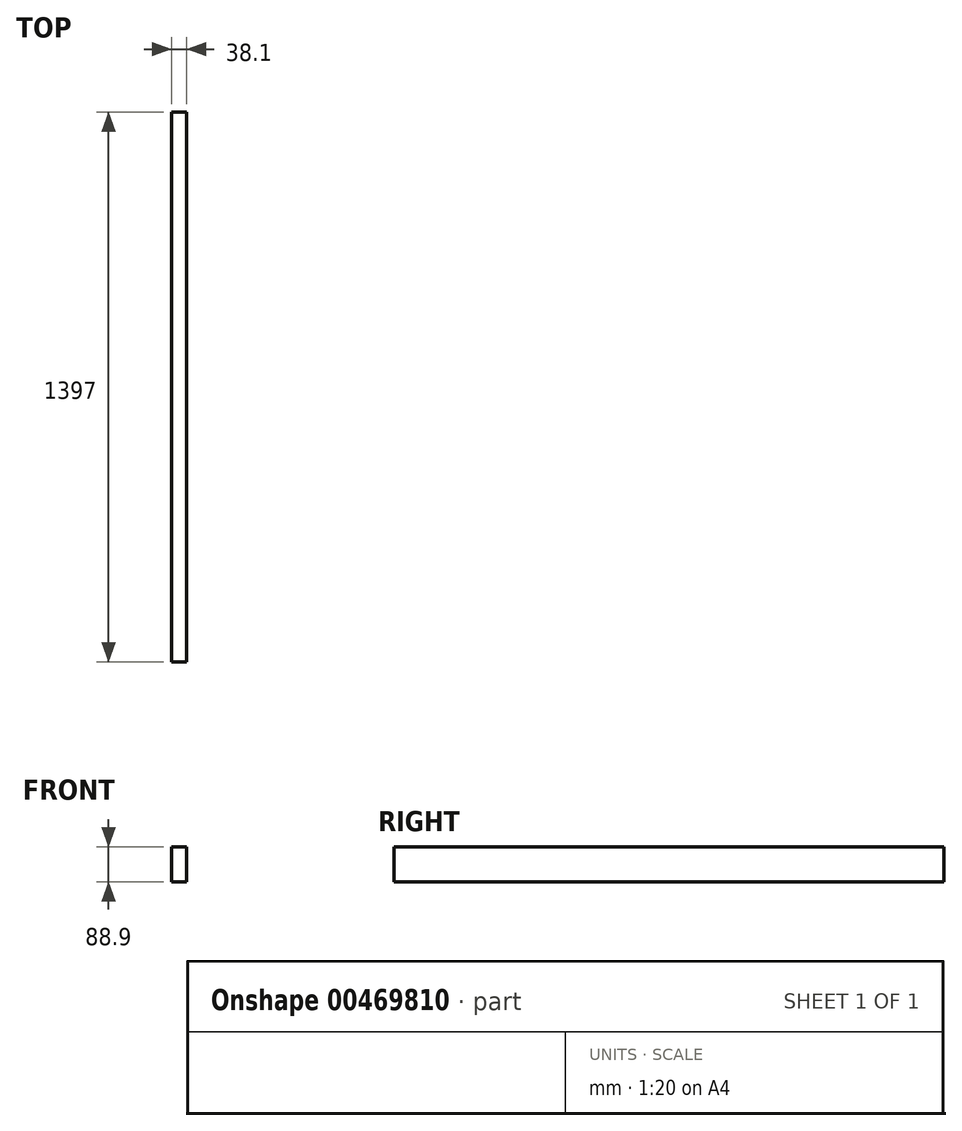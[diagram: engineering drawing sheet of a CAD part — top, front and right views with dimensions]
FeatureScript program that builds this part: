
annotation { "Feature Type Name" : "Feature", "Feature Type Description" : "" }
export const myFeature = defineFeature(function(context is Context, id is Id, definition is map)
    precondition{}
    {
        {
            var Q0;
            Q0=qCreatedBy(makeId("Front.planeOp"),FACE);
            var sketch = newSketch(context, id + "F0", { "sketchPlane" : qUnion([Q0])});
            skLineSegment(sketch, "E0.bottom", {"start": v(19.05, 44.45) * mm, "end": v(-19.05, 44.45) * mm});
            skLineSegment(sketch, "E0.top", {"start": v(19.05, -44.45) * mm, "end": v(-19.05, -44.45) * mm});
            skLineSegment(sketch, "E0.left", {"start": v(19.05, 44.45) * mm, "end": v(19.05, -44.45) * mm});
            skLineSegment(sketch, "E0.right", {"start": v(-19.05, 44.45) * mm, "end": v(-19.05, -44.45) * mm});
            skPoint(sketch, "E0.middle", {"position": v(0, 0) * mm});
            skSolve(sketch);
        }
        {
            var Q0;
            Q0=qSketchRegion(id+"F0",true);
            extrude(context, id + "F1", {"entities" : qUnion([Q0]), "oppositeDirection" : true, "depth" : 1397 * mm});
        }
    });
